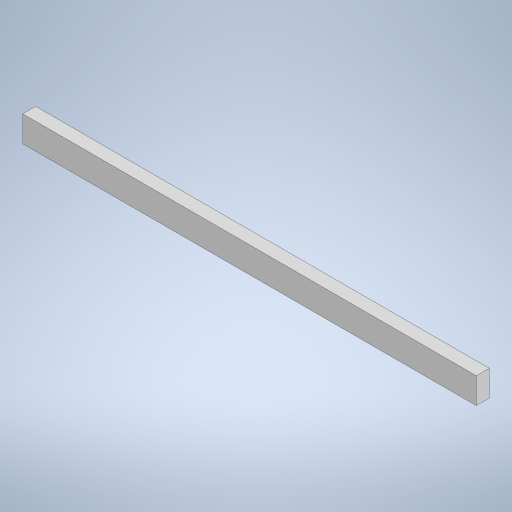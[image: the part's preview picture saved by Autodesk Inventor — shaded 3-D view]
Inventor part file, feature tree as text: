
AUTODESK INVENTOR PART (.ipt)
format: ipt  version: 2024 (Build 280153000, 153)  size: 248,832 bytes
history: native  units: mm
features: extrude x4, sketch x4, projected_geometry x3
ambient origin geometry x8: Origin, YZ Plane, XZ Plane, XY Plane, X Axis, Y Axis, Z Axis, Center Point
bodies: Solid1 (feature_tree)
feature tree (11):
  extrude  "Extrusion1"  Depth=5.0mm TaperAngle=0.0deg
  extrude  "Extrusion2"  Depth=25.0mm TaperAngle=0.0deg
  extrude  "Extrusion3"  [1 undecoded]
  extrude  "Extrusion4"  [1 undecoded]
  sketch  "Sketch1"  dims[d2=5.0mm d3=0.0mm d4=150.0mm d5=0.0mm]
  sketch  "Sketch2"  dims[d6=50.0mm d7=0.0mm d8=25.0mm d9=0.0mm]
  projected_geometry  "Projected Loop1"
  sketch  "Sketch3"
  projected_geometry  "Projected Loop2"
  sketch  "Sketch4"
  projected_geometry  "Projected Loop3"
note: 2 required parameter values undecoded (feature->parameter linkage not recoverable at this tier; creation-order binding heuristic only, values carry confidence <= 0.55)
